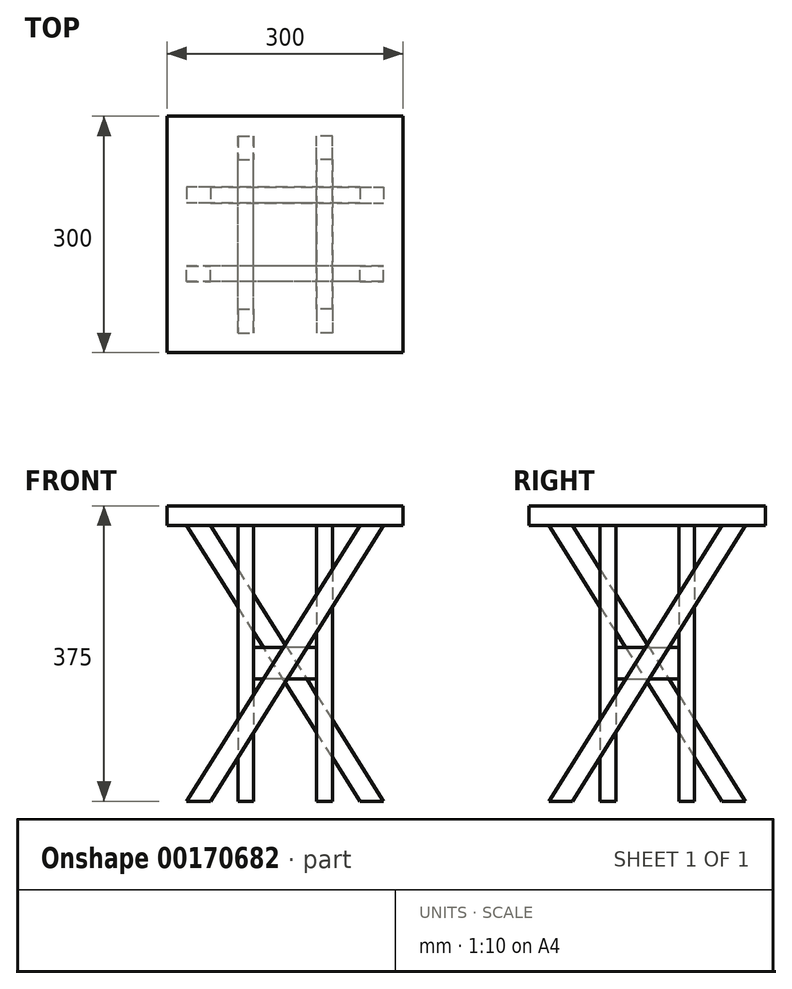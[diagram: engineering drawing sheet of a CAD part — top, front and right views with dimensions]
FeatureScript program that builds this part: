
annotation { "Feature Type Name" : "Feature", "Feature Type Description" : "" }
export const myFeature = defineFeature(function(context is Context, id is Id, definition is map)
    precondition{}
    {
        {
            var Q0;
            Q0=qCreatedBy(makeId("Top.planeOp"),FACE);
            var sketch = newSketch(context, id + "F0", { "sketchPlane" : qUnion([Q0])});
            skLineSegment(sketch, "E0.bottom", {"start": v(150, -150) * mm, "end": v(-150, -150) * mm});
            skLineSegment(sketch, "E0.top", {"start": v(150, 150) * mm, "end": v(-150, 150) * mm});
            skLineSegment(sketch, "E0.left", {"start": v(150, -150) * mm, "end": v(150, 150) * mm});
            skLineSegment(sketch, "E0.right", {"start": v(-150, -150) * mm, "end": v(-150, 150) * mm});
            skPoint(sketch, "E0.middle", {"position": v(0, 0) * mm});
            skLineSegment(sketch, "E1.bottom", {"start": v(40, -40) * mm, "end": v(-40, -40) * mm});
            skLineSegment(sketch, "E1.top", {"start": v(40, 40) * mm, "end": v(-40, 40) * mm});
            skLineSegment(sketch, "E1.left", {"start": v(40, -40) * mm, "end": v(40, 40) * mm});
            skLineSegment(sketch, "E1.right", {"start": v(-40, -40) * mm, "end": v(-40, 40) * mm});
            skSolve(sketch);
        }
        {
            var Q0;
            Q0=qCreatedBy(makeId("Front.planeOp"),FACE);
            var sketch = newSketch(context, id + "F1", { "sketchPlane" : qUnion([Q0])});
            skLineSegment(sketch, "E2.bottom", {"start": v(-125, 0) * mm, "end": v(125, 0) * mm, "construction": true});
            skLineSegment(sketch, "E2.top", {"start": v(-125, -350) * mm, "end": v(125, -350) * mm, "construction": true});
            skLineSegment(sketch, "E2.left", {"start": v(-125, 0) * mm, "end": v(-125, -350) * mm, "construction": true});
            skLineSegment(sketch, "E2.right", {"start": v(125, 0) * mm, "end": v(125, -350) * mm, "construction": true});
            skLineSegment(sketch, "E3", {"start": v(0, 0) * mm, "end": v(0, -350) * mm, "construction": true});
            skLineSegment(sketch, "E4", {"start": v(125, 0) * mm, "end": v(-125, -350) * mm, "construction": true});
            skLineSegment(sketch, "E5", {"start": v(-125, 0) * mm, "end": v(125, -350) * mm, "construction": true});
            skLineSegment(sketch, "E6", {"start": v(-95, 0) * mm, "end": v(125, -350) * mm});
            skLineSegment(sketch, "E7", {"start": v(95, -350) * mm, "end": v(-125, 0) * mm});
            skLineSegment(sketch, "E8", {"start": v(95, 0) * mm, "end": v(-125, -350) * mm});
            skLineSegment(sketch, "E9", {"start": v(125, 0) * mm, "end": v(-95, -350) * mm});
            skLineSegment(sketch, "E10", {"start": v(-125, -350) * mm, "end": v(-95, -350) * mm});
            skLineSegment(sketch, "E11", {"start": v(95, -350) * mm, "end": v(125, -350) * mm});
            skLineSegment(sketch, "E12", {"start": v(95, 0) * mm, "end": v(125, 0) * mm});
            skLineSegment(sketch, "E13", {"start": v(-95, 0) * mm, "end": v(-125, 0) * mm});
            skLineSegment(sketch, "E14", {"start": v(0, -175) * mm, "end": v(36.92, -175) * mm, "construction": true});
            skPoint(sketch, "E14.endSnap0", {"position": v(0, -175) * mm});
            skSolve(sketch);
        }
        {
            var Q0;
            Q0=makeQuery(id+"F0.imprint","IMPRINT",FACE,{"disambiguationData":[TD([[makeQuery(id+"F0.imprint","IMPRINT",EDGE,{"derivedFrom":sQuery(id+"F0.wireOp",EDGE,"E0.bottom")}),-1.0]])]});
            var Q1;
            Q1=sQuery(id+"F1.wireOp",EDGE,"E14");
            cPlane(context, id + "F2", {"entities" : qUnion([Q0, Q1]), "cplaneType" : CPlaneType.LINE_ANGLE, "offset" : 25 * mm, "angle" : 0 * degree, "width" : 150 * mm, "height" : 150 * mm});
        }
        {
            var Q0;
            Q0=qCreatedBy(id+"F2.planeOp",FACE);
            var sketch = newSketch(context, id + "F3", { "sketchPlane" : qUnion([Q0])});
            skLineSegment(sketch, "E15.0", {"start": v(-40, 40) * mm, "end": v(-40, -40) * mm});
            skLineSegment(sketch, "E15.1", {"start": v(40, -40) * mm, "end": v(-40, -40) * mm});
            skLineSegment(sketch, "E15.2", {"start": v(40, 40) * mm, "end": v(-40, 40) * mm});
            skLineSegment(sketch, "E15.3", {"start": v(40, 40) * mm, "end": v(40, -40) * mm});
            skSolve(sketch);
        }
        {
            var Q0;
            Q0=qCreatedBy(makeId("Front.planeOp"),FACE);
            var Q1;
            Q1=sQuery(id+"F3.wireOp",EDGE,"E15.1");
            cPlane(context, id + "F4", {"entities" : qUnion([Q0, Q1]), "cplaneType" : CPlaneType.LINE_ANGLE, "offset" : 25 * mm, "angle" : 0 * degree, "width" : 150 * mm, "height" : 150 * mm});
        }
        {
            var Q0;
            Q0=qCreatedBy(makeId("Front.planeOp"),FACE);
            var Q1;
            Q1=sQuery(id+"F3.wireOp",EDGE,"E15.2");
            cPlane(context, id + "F5", {"entities" : qUnion([Q0, Q1]), "cplaneType" : CPlaneType.LINE_ANGLE, "offset" : 25 * mm, "angle" : 0 * degree, "width" : 150 * mm, "height" : 150 * mm});
        }
        {
            var Q0;
            Q0=qCreatedBy(id+"F4.planeOp",FACE);
            var sketch = newSketch(context, id + "F6", { "sketchPlane" : qUnion([Q0])});
            skLineSegment(sketch, "E16.0", {"start": v(-95, -350) * mm, "end": v(125, 0) * mm});
            skLineSegment(sketch, "E16.1", {"start": v(95, 0) * mm, "end": v(-125, -350) * mm});
            skLineSegment(sketch, "E16.2", {"start": v(95, 0) * mm, "end": v(125, 0) * mm});
            skLineSegment(sketch, "E16.3", {"start": v(-95, -350) * mm, "end": v(-125, -350) * mm});
            skSolve(sketch);
        }
        {
            var Q0;
            Q0=qCreatedBy(id+"F5.planeOp",FACE);
            var sketch = newSketch(context, id + "F7", { "sketchPlane" : qUnion([Q0])});
            skLineSegment(sketch, "E17.0", {"start": v(-95, 0) * mm, "end": v(-125, 0) * mm});
            skLineSegment(sketch, "E17.1", {"start": v(-125, 0) * mm, "end": v(95, -350) * mm});
            skLineSegment(sketch, "E17.2", {"start": v(-95, 0) * mm, "end": v(125, -350) * mm});
            skLineSegment(sketch, "E17.3", {"start": v(125, -350) * mm, "end": v(95, -350) * mm});
            skSolve(sketch);
        }
        {
            var Q0;
            Q0=makeQuery(id+"F7.imprint","IMPRINT",FACE,{"disambiguationData":[TD([[makeQuery(id+"F7.imprint","IMPRINT",EDGE,{"derivedFrom":sQuery(id+"F7.wireOp",EDGE,"E17.0")}),1.0]])]});
            extrude(context, id + "F8", {"entities" : qUnion([Q0]), "oppositeDirection" : true, "depth" : 20 * mm});
        }
        {
            var Q0;
            Q0=makeQuery(id+"F6.imprint","IMPRINT",FACE,{"disambiguationData":[TD([[makeQuery(id+"F6.imprint","IMPRINT",EDGE,{"derivedFrom":sQuery(id+"F6.wireOp",EDGE,"E16.0")}),1.0]])]});
            extrude(context, id + "F9", {"entities" : qUnion([Q0]), "depth" : 20 * mm});
        }
        {
            var Q0;
            Q0=makeQuery(id+"F8.opExtrude","SWEPT_BODY",BODY,{"disambiguationData":[OSD([sQuery(id+"F7.wireOp",EDGE,"E17.0"),sQuery(id+"F7.wireOp",EDGE,"E17.1"),sQuery(id+"F7.wireOp",EDGE,"E17.2"),sQuery(id+"F7.wireOp",EDGE,"E17.3")])]});
            var Q1;
            Q1=makeQuery(id+"F9.opExtrude","SWEPT_BODY",BODY,{"disambiguationData":[OSD([sQuery(id+"F6.wireOp",EDGE,"E16.0"),sQuery(id+"F6.wireOp",EDGE,"E16.1"),sQuery(id+"F6.wireOp",EDGE,"E16.2"),sQuery(id+"F6.wireOp",EDGE,"E16.3")])]});
            var Q2;
            Q2=sQuery(id+"F1.wireOp",EDGE,"E3");
            circularPattern(context, id + "F10", {"entities" : qUnion([Q0, Q1]), "axis" : qUnion([Q2]), "angle" : 90 * degree, "instanceCount" : 2});
        }
        {
            var Q0;
            Q0=makeQuery(id+"F3.imprint","IMPRINT",FACE,{"disambiguationData":[TD([[makeQuery(id+"F3.imprint","IMPRINT",EDGE,{"derivedFrom":sQuery(id+"F3.wireOp",EDGE,"E15.0")}),1.0]])]});
            extrude(context, id + "F11", {"entities" : qUnion([Q0]), "depth" : 40 * mm, "symmetric" : true});
        }
        {
            var Q0;
            Q0=makeQuery(id+"F0.imprint","IMPRINT",FACE,{"disambiguationData":[TD([[makeQuery(id+"F0.imprint","IMPRINT",EDGE,{"derivedFrom":sQuery(id+"F0.wireOp",EDGE,"E0.bottom")}),-1.0]])]});
            var Q1;
            Q1=makeQuery(id+"F0.imprint","IMPRINT",FACE,{"disambiguationData":[TD([[makeQuery(id+"F0.imprint","IMPRINT",EDGE,{"derivedFrom":sQuery(id+"F0.wireOp",EDGE,"E1.bottom")}),-1.0]])]});
            extrude(context, id + "F12", {"entities" : qUnion([Q0, Q1]), "depth" : 25 * mm});
        }
    });
